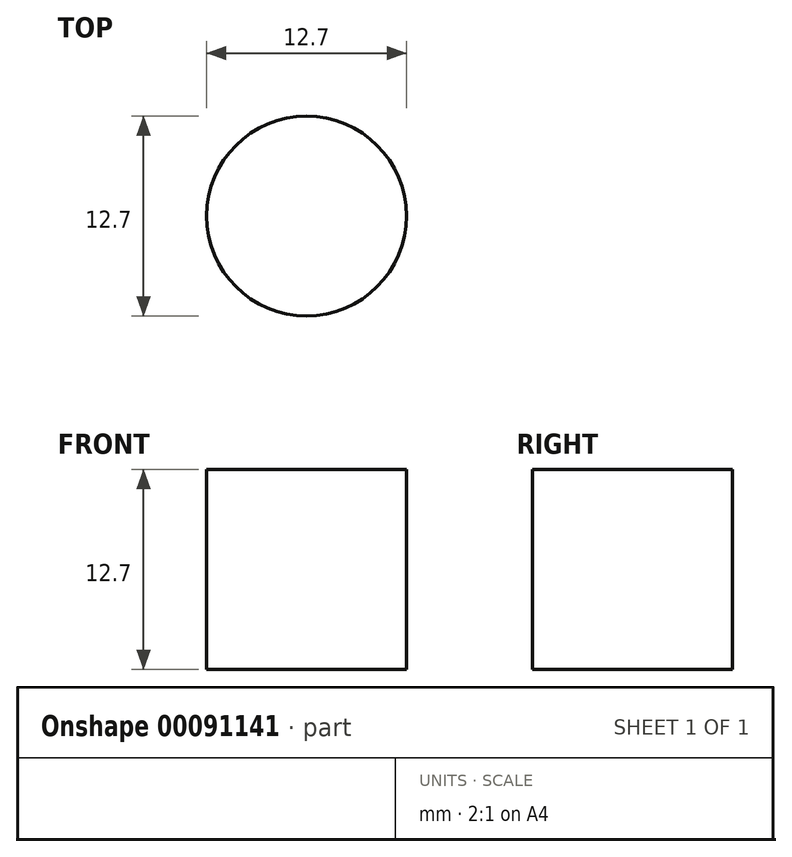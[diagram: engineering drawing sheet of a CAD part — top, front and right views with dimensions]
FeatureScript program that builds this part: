
annotation { "Feature Type Name" : "Feature", "Feature Type Description" : "" }
export const myFeature = defineFeature(function(context is Context, id is Id, definition is map)
    precondition{}
    {
        {
            var Q0;
            Q0=qCreatedBy(makeId("Top.planeOp"),FACE);
            var sketch = newSketch(context, id + "F0", { "sketchPlane" : qUnion([Q0])});
            skCircle(sketch, "E0", {"center": v(0, 0) * mm, "radius": 6.35 * mm});
            skSolve(sketch);
        }
        {
            var Q0;
            Q0 = qSketchRegion(id + "F0", true);
            extrude(context, id + "F1", {"entities" : qUnion([Q0]), "depth" : 12.7 * mm});
        }
    });
